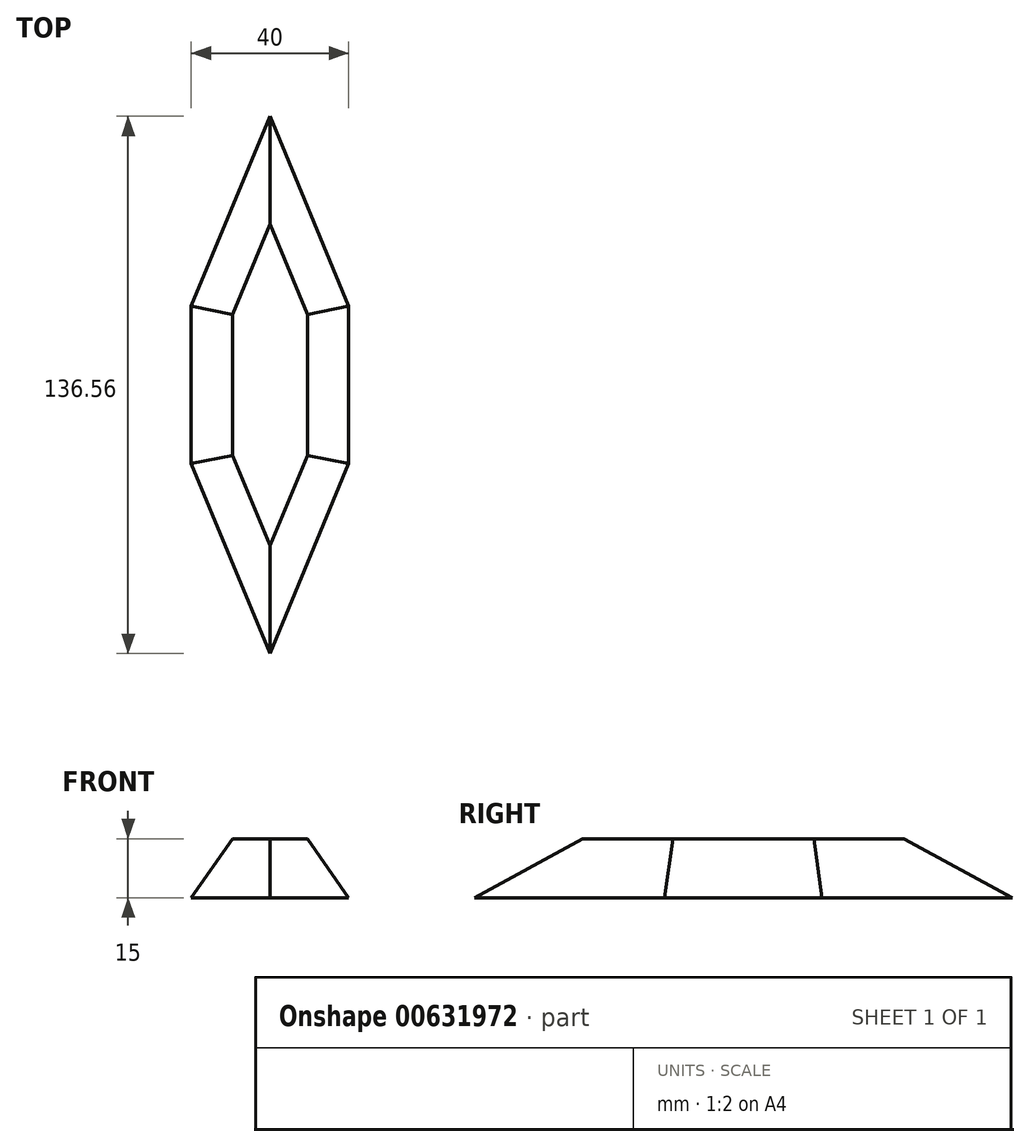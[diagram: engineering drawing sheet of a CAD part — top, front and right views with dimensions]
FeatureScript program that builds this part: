
annotation { "Feature Type Name" : "Feature", "Feature Type Description" : "" }
export const myFeature = defineFeature(function(context is Context, id is Id, definition is map)
    precondition{}
    {
        {
            var Q0;
            Q0=qCreatedBy(makeId("Top.planeOp"),FACE);
            var sketch = newSketch(context, id + "F0", { "sketchPlane" : qUnion([Q0])});
            skLineSegment(sketch, "E0.bottom", {"start": v(-20, 20) * mm, "end": v(20, 20) * mm});
            skLineSegment(sketch, "E0.top", {"start": v(-20, -20) * mm, "end": v(20, -20) * mm});
            skLineSegment(sketch, "E0.left", {"start": v(-20, 20) * mm, "end": v(-20, -20) * mm});
            skLineSegment(sketch, "E0.right", {"start": v(20, 20) * mm, "end": v(20, -20) * mm});
            skPoint(sketch, "E1", {"position": v(0, 20) * mm});
            skLineSegment(sketch, "E2", {"start": v(0, 20) * mm, "end": v(0, 0) * mm, "construction": true});
            skLineSegment(sketch, "E3", {"start": v(-20, 0) * mm, "end": v(0, 0) * mm, "construction": true});
            skLineSegment(sketch, "E4", {"start": v(-20, 20) * mm, "end": v(0, 68.28) * mm});
            skLineSegment(sketch, "E5", {"start": v(0, 68.28) * mm, "end": v(20, 20) * mm});
            skLineSegment(sketch, "E6", {"start": v(-20, -20) * mm, "end": v(0, -68.28) * mm});
            skLineSegment(sketch, "E7", {"start": v(20, -20) * mm, "end": v(0, -68.28) * mm});
            skSolve(sketch);
        }
        {
            var Q0;
            Q0 = qSketchRegion(id + "F0", true);
            extrude(context, id + "F1", {"entities" : qUnion([Q0]), "depth" : 15 * mm, "offsetDistance" : 25 * mm, "hasDraft" : true, "draftAngle" : 35 * degree, "draftPullDirection" : true});
        }
    });
